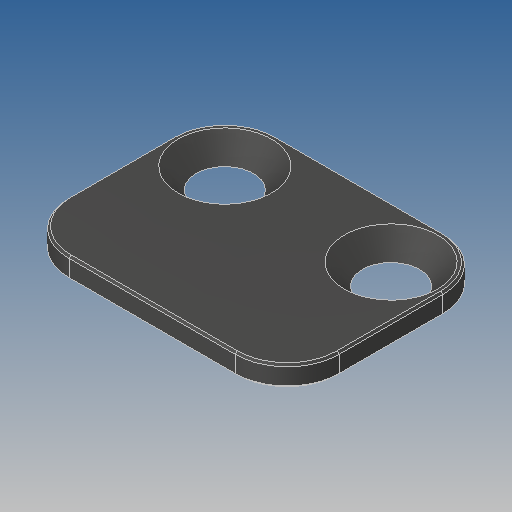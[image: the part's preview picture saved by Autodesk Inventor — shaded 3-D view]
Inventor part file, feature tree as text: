
AUTODESK INVENTOR PART (.ipt)
format: ipt  version: 2019 (Build 230136000, 136)  size: 118,784 bytes
history: native  units: mm
features: chamfer x1
ambient origin geometry x8: Origin, YZ Plane, XZ Plane, XY Plane, X Axis, Y Axis, Z Axis, Center Point
bodies: Solid1 (feature_tree)
feature tree (1):
  chamfer  "Chamfer1"  [1 undecoded]
note: 1 required parameter value undecoded (feature->parameter linkage not recoverable at this tier; creation-order binding heuristic only, values carry confidence <= 0.55)
